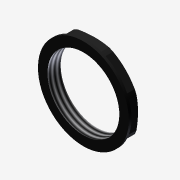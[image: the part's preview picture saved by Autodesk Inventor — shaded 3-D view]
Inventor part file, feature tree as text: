
AUTODESK INVENTOR PART (.ipt)
format: ipt  version: 2014 (Build 180170000, 170)  size: 108,032 bytes
history: native  units: mm
features: imported_body x1, thread x1
ambient origin geometry x8: Origin, YZ Plane, XZ Plane, XY Plane, X Axis, Y Axis, Z Axis, Center Point
bodies: Solid1 (feature_tree)
feature tree (2):
  imported_body  "Base1"
  thread  "Thread1"  [1 undecoded]
note: 1 required parameter value undecoded (feature->parameter linkage not recoverable at this tier; creation-order binding heuristic only, values carry confidence <= 0.55)
